# Revit family: NLRS_21_SF_FB_boutanker 1988 M16x140_VPB
name_source: partatom
category: Structural Framing
units: mm (PartAtom-declared; Revit-internal decimal feet)

## family parameters
Always export as geometry = Yes
Cut with Voids When Loaded = No
Host = Face
Material for Model Behavior = Steel
Section Shape = Not Defined
Shared = Yes
Show family pre-cut in plan views = No

## types (1)
- 123Casco_VPB_M16x140
    Assembly Code = 21.21
    Default Elevation = 0 mm  [stored 0 ft]
    Description = Boutanker 1988 M16x145 mm
    Instortvoorziening = Yes
    L = 140 mm  [stored 0.459318 ft]
    Manufacturer = 123Casco
    Model = Voorbij-B-Anker
    Posnummer = 300187
    Structural Material = <By Category>
    Type Comments = Boutanker 1988 M16x145 mm
    a = 31 mm
    b = 21 mm
    dnom = 16 mm
    halve_b = 11 mm
    halve_dnom = 8 mm  [stored 0.0262467 ft]
    halve_f = 10 mm  [stored 0.0328084 ft]

note: [stored X ft] marks values corroborated as IEEE doubles in the binary element streams (Revit-internal decimal feet)

## geometry (parser evidence)
native form markers: Blend x18, Sweep x2
no freeform markers — native parametric forms only
